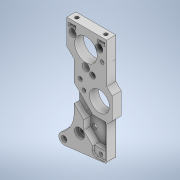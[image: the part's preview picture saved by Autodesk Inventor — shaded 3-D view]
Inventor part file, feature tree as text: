
AUTODESK INVENTOR PART (.ipt)
format: ipt  version: 2020 (Build 240168000, 168)  size: 537,600 bytes
history: native  units: mm
features: extrude x14, sketch x10, fillet x5, projected_geometry x5, thread x2, chamfer x1
ambient origin geometry x8: Origin, YZ Plane, XZ Plane, XY Plane, X Axis, Y Axis, Z Axis, Center Point
bodies: Solid1 (feature_tree)
feature tree (37):
  extrude  "Extrusion1"  Depth=23.5mm
  fillet  "Fillet1"  Radius=23.5mm
  fillet  "Fillet2"  Radius=6.0mm
  extrude  "Extrusion2"  Depth=3.0mm
  extrude  "Extrusion3"  Depth=4.0mm
  thread  "Thread1"  [1 undecoded]
  thread  "Thread2"  [1 undecoded]
  extrude  "Extrusion4"  Depth=24.75mm
  extrude  "Extrusion5"  Depth=2.1mm
  extrude  "Extrusion6"  Depth=4.0mm
  extrude  "Extrusion7"  TaperAngle=45.0deg  [1 undecoded]
  extrude  "Extrusion8"  Depth=12.0mm
  extrude  "Extrusion9"  TaperAngle=135.0deg  [1 undecoded]
  extrude  "Extrusion10"  Depth=5.0mm TaperAngle=0.0deg
  fillet  "Fillet3"  Radius=3.0mm
  extrude  "Extrusion11"  Depth=10.0mm
  chamfer  "Chamfer1"  Distance=3.0mm
  fillet  "Fillet4"  Radius=2.5mm
  extrude  "Extrusion12"  Depth=0.5mm
  extrude  "Extrusion13"  Depth=7.5mm
  extrude  "Extrusion14"  Depth=0.5mm
  fillet  "Fillet5"  Radius=15.0mm
  sketch  "Sketch3"  dims[d0=3.0mm d1=6.0mm d2=23.5mm d3=6.0mm]
  projected_geometry  "Projected Loop1"
  sketch  "Sketch5"  dims[d4=0.0mm d5=3.0mm]
  sketch  "Sketch7"  dims[d6=18.0mm d7=56.0mm d8=11.0mm d9=4.0mm]
  sketch  "Sketch8"  dims[d10=24.75mm d11=12.5mm]
  projected_geometry  "Projected Loop2"
  sketch  "Sketch10"  dims[d12=22.3mm d14=2.1mm]
  sketch  "Sketch13"  dims[d18=30.0mm d20=360.0deg d22=4.0mm]
  sketch  "Sketch15"  dims[d23=14.0mm d24=45.0deg]
  sketch  "Sketch17"  dims[d25=3.0mm d26=12.0mm]
  projected_geometry  "Projected Loop3"
  sketch  "Sketch21"  dims[d27=6.0mm d28=135.0deg]
  projected_geometry  "Projected Loop5"
  sketch  "Sketch22"  dims[d29=135.0deg d30=5.0mm d31=0.0mm d32=3.0mm d33=10.0mm d34=3.0mm d35=2.5mm d36=13.5mm d37=7.5mm d38=2.5mm d39=15.0mm d40=12.5mm d41=1.0mm d42=15.0mm d43=12.75mm d44=20.0mm d45=23.75mm d46=3.0mm d47=0.0mm d48=2.0mm d49=2.0mm d50=2.5mm d51=2.5mm d52=3.0mm d53=3.0mm d54=4.5mm d55=0.0mm d56=7.0mm d57=0.0mm d58=7.0mm d59=0.0mm d60=8.5mm d61=270.0deg d62=4.0mm d63=4.0mm d64=4.0mm d65=3.0mm d66=0.0mm d67=5.5mm d68=2.0mm d69=0.0mm d70=4.0mm d71=1.85mm d72=4.0mm d73=1.85mm d74=1.0mm d75=2.8mm d76=2.8mm d77=1.0mm d78=10.0mm d79=0.0mm d82=3.1mm d83=11.15mm d84=2.1mm d85=2.1mm d86=2.1mm d87=5.5mm d88=3.5mm d89=25.75mm d90=30.25mm d91=2.5mm d92=11.75mm d93=24.0mm d94=8.0mm d95=2.1mm d96=2.1mm d98=2.1mm d99=1.8mm d100=0.0mm d101=2.1mm d102=2.1mm d103=2.1mm d104=1.8mm d105=0.0mm d117=3.9mm d118=0.0mm d119=18.0mm d120=6.5mm d121=0.0mm d122=1.0mm d125=5.0mm d126=7.25mm d127=2.5mm d128=5.0mm d129=15.0mm d130=5.0mm d131=5.0mm d132=90.0deg d133=135.0deg d135=135.0deg d136=135.0deg d137=3.0mm d138=0.0mm d139=0.9mm d140=2.0mm d141=45.0deg d142=4.0mm d143=2.0mm d144=2.6mm d145=3.625mm d146=10.0mm d147=0.0mm d148=2.05mm d149=2.4mm d150=0.0mm d151=4.5mm d154=1.0mm d155=0.0mm d156=2.0mm d157=2.8mm d80=0.5mm d81=0.872665mm d106=0.872665mm d123=0.872665mm d134=0.5mm d153=0.5mm]
  projected_geometry  "Projected Loop6"
note: 4 required parameter values undecoded (feature->parameter linkage not recoverable at this tier; creation-order binding heuristic only, values carry confidence <= 0.55)
